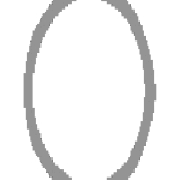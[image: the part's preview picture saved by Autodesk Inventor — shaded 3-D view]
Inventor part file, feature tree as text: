
AUTODESK INVENTOR PART (.ipt)
format: ipt  version: 2021 (Build 250183000, 183)  size: 115,200 bytes
history: native  units: in
note: dims shown in document units (in); Inventor stores cm internally (conversion verified against a paired STEP export)
features: other x4, sketch x3, plane x1
ambient origin geometry x8: Origin, YZ Plane, XZ Plane, XY Plane, X Axis, Y Axis, Z Axis, Center Point
bodies: Solid1 (feature_tree), Body (feature_tree)
feature tree (8):
  other  "Driven Length"
  other  "Frame Generator"
  other  "Start Plane"
  other  "End Plane"
  sketch  "Sketch"  dims[d2=1.5435in d4=-0.0in d5=1.5435in d6=0.12in d7=0.0in d8=90.0deg d9=1.5435in]
  sketch  "Sketch2"  dims[d0=1.0in]
  plane  "Work Plane3"
  sketch  "Sketch3"  dims[d1=0.065in]
